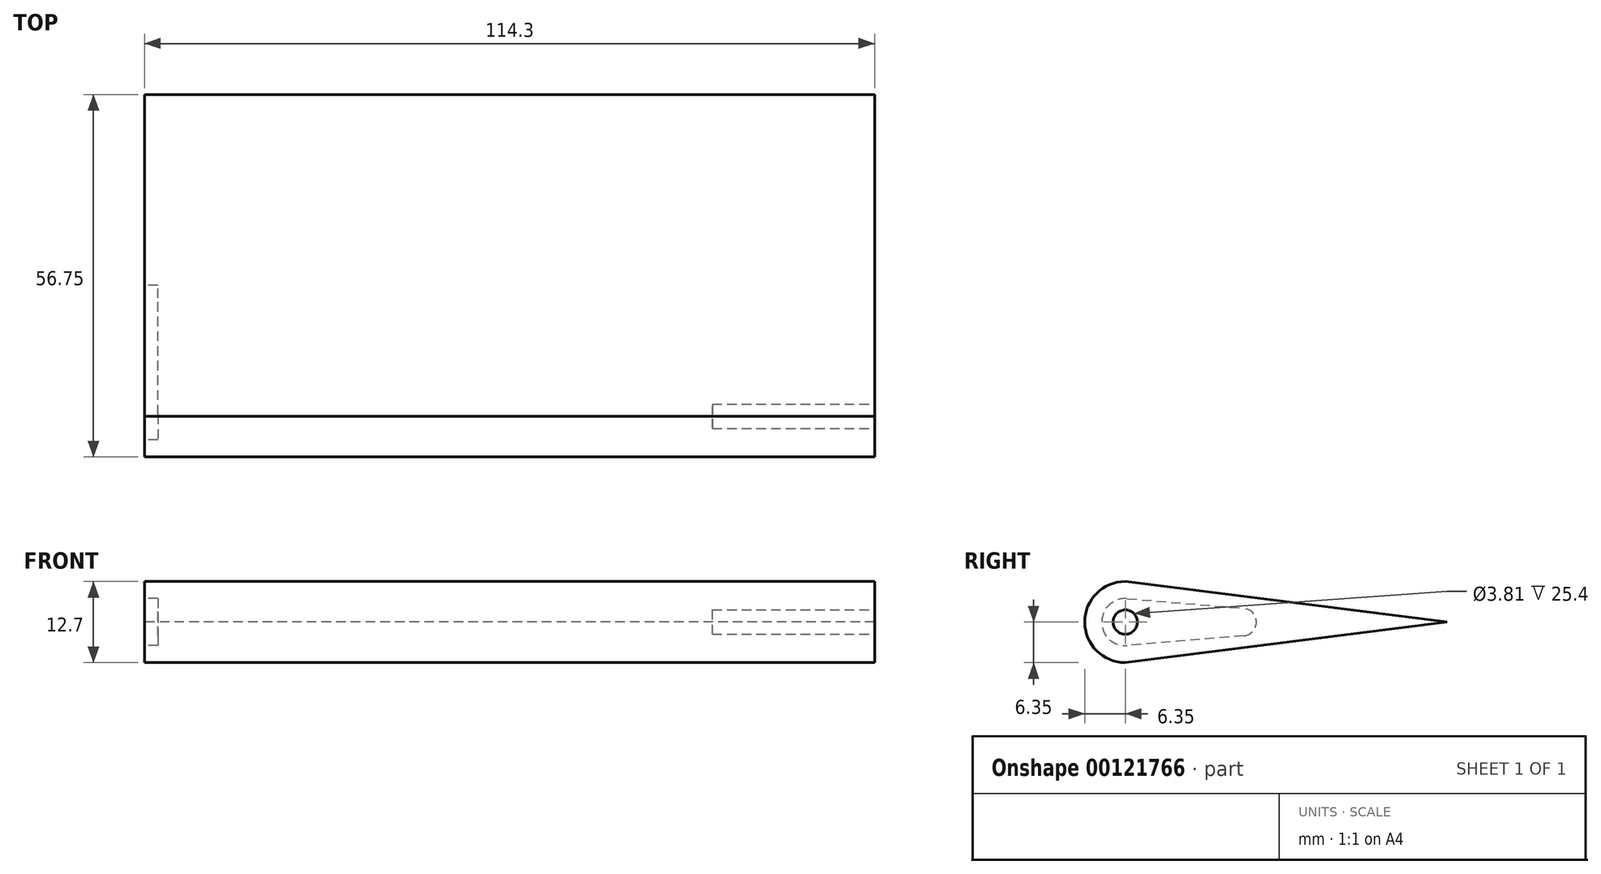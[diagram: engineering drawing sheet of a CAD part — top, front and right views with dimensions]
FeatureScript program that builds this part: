
annotation { "Feature Type Name" : "Feature", "Feature Type Description" : "" }
export const myFeature = defineFeature(function(context is Context, id is Id, definition is map)
    precondition{}
    {
        {
            var Q0;
            Q0=qCreatedBy(makeId("Right.planeOp"),FACE);
            var sketch = newSketch(context, id + "F0", { "sketchPlane" : qUnion([Q0])});
            skArc(sketch, "E0", {"start": v(0.28, 3.42) * mm, "mid": v(-3.43, 0) * mm, "end": v(0.28, -3.42) * mm, "construction": true});
            skArc(sketch, "E1", {"start": v(18.52, -1.9) * mm, "mid": v(20.27, 0) * mm, "end": v(18.52, 1.9) * mm, "construction": true});
            skLineSegment(sketch, "E2", {"start": v(0.28, 3.42) * mm, "end": v(18.52, 1.9) * mm, "construction": true});
            skLineSegment(sketch, "E3", {"start": v(18.52, -1.9) * mm, "end": v(0.28, -3.42) * mm, "construction": true});
            skCircle(sketch, "E4", {"center": v(0, 0) * mm, "radius": 1.27 * mm, "construction": true});
            skArc(sketch, "E5", {"start": v(0, 6.35) * mm, "mid": v(-6.35, 0) * mm, "end": v(0, -6.35) * mm});
            skLineSegment(sketch, "E6", {"start": v(0, 6.35) * mm, "end": v(50.4, 0) * mm});
            skLineSegment(sketch, "E7", {"start": v(50.4, 0) * mm, "end": v(0, -6.35) * mm});
            skLineSegment(sketch, "E8.0", {"start": v(0.3, 3.67) * mm, "end": v(18.54, 2.15) * mm});
            skArc(sketch, "E8.1", {"start": v(0.3, 3.67) * mm, "mid": v(-3.68, 0) * mm, "end": v(0.3, -3.67) * mm});
            skLineSegment(sketch, "E8.2", {"start": v(18.54, -2.15) * mm, "end": v(0.3, -3.67) * mm});
            skArc(sketch, "E8.3", {"start": v(18.54, -2.15) * mm, "mid": v(20.52, 0) * mm, "end": v(18.54, 2.15) * mm});
            skCircle(sketch, "E9.0", {"center": v(0, 0) * mm, "radius": 2.86 * mm});
            skSolve(sketch);
        }
        {
            var Q0;
            Q0=makeQuery(id+"F0.imprint","IMPRINT",FACE,{"disambiguationData":[TD([[makeQuery(id+"F0.imprint","IMPRINT",EDGE,{"derivedFrom":sQuery(id+"F0.wireOp",EDGE,"E5")}),1.0]])]});
            var Q1;
            Q1=makeQuery(id+"F0.imprint","IMPRINT",FACE,{"disambiguationData":[TD([[makeQuery(id+"F0.imprint","IMPRINT",EDGE,{"derivedFrom":sQuery(id+"F0.wireOp",EDGE,"E8.0")}),-1.0]])]});
            var Q2;
            Q2=makeQuery(id+"F0.imprint","IMPRINT",FACE,{"disambiguationData":[TD([[makeQuery(id+"F0.imprint","IMPRINT",EDGE,{"derivedFrom":sQuery(id+"F0.wireOp",EDGE,"E9.0")}),1.0]])]});
            extrude(context, id + "F1", {"entities" : qUnion([Q0, Q1, Q2]), "depth" : 114.3 * mm});
        }
        {
            var Q0;
            Q0=makeQuery(id+"F0.imprint","IMPRINT",FACE,{"disambiguationData":[TD([[makeQuery(id+"F0.imprint","IMPRINT",EDGE,{"derivedFrom":sQuery(id+"F0.wireOp",EDGE,"E8.0")}),-1.0]])]});
            var Q1;
            Q1=makeQuery(id+"F0.imprint","IMPRINT",FACE,{"disambiguationData":[TD([[makeQuery(id+"F0.imprint","IMPRINT",EDGE,{"derivedFrom":sQuery(id+"F0.wireOp",EDGE,"E9.0")}),1.0]])]});
            extrude(context, id + "F2", {"entities" : qUnion([Q0, Q1]), "operationType" : NewBodyOperationType.REMOVE, "depth" : 2.08 * mm});
        }
        {
            var Q0;
            Q0=makeQuery(id+"F1.opExtrude","CAP_FACE",FACE,{"disambiguationData":[OSD([sQuery(id+"F0.wireOp",EDGE,"E5"),sQuery(id+"F0.wireOp",EDGE,"E6"),sQuery(id+"F0.wireOp",EDGE,"E7")])],"isStart":false});
            var sketch = newSketch(context, id + "F3", { "sketchPlane" : qUnion([Q0])});
            skCircle(sketch, "E10", {"center": v(0, 0) * mm, "radius": 1.9 * mm});
            skSolve(sketch);
        }
        {
            var Q0;
            Q0 = qSketchRegion(id + "F3", true);
            extrude(context, id + "F4", {"entities" : qUnion([Q0]), "operationType" : NewBodyOperationType.REMOVE, "oppositeDirection" : true, "depth" : 25.4 * mm});
        }
    });
